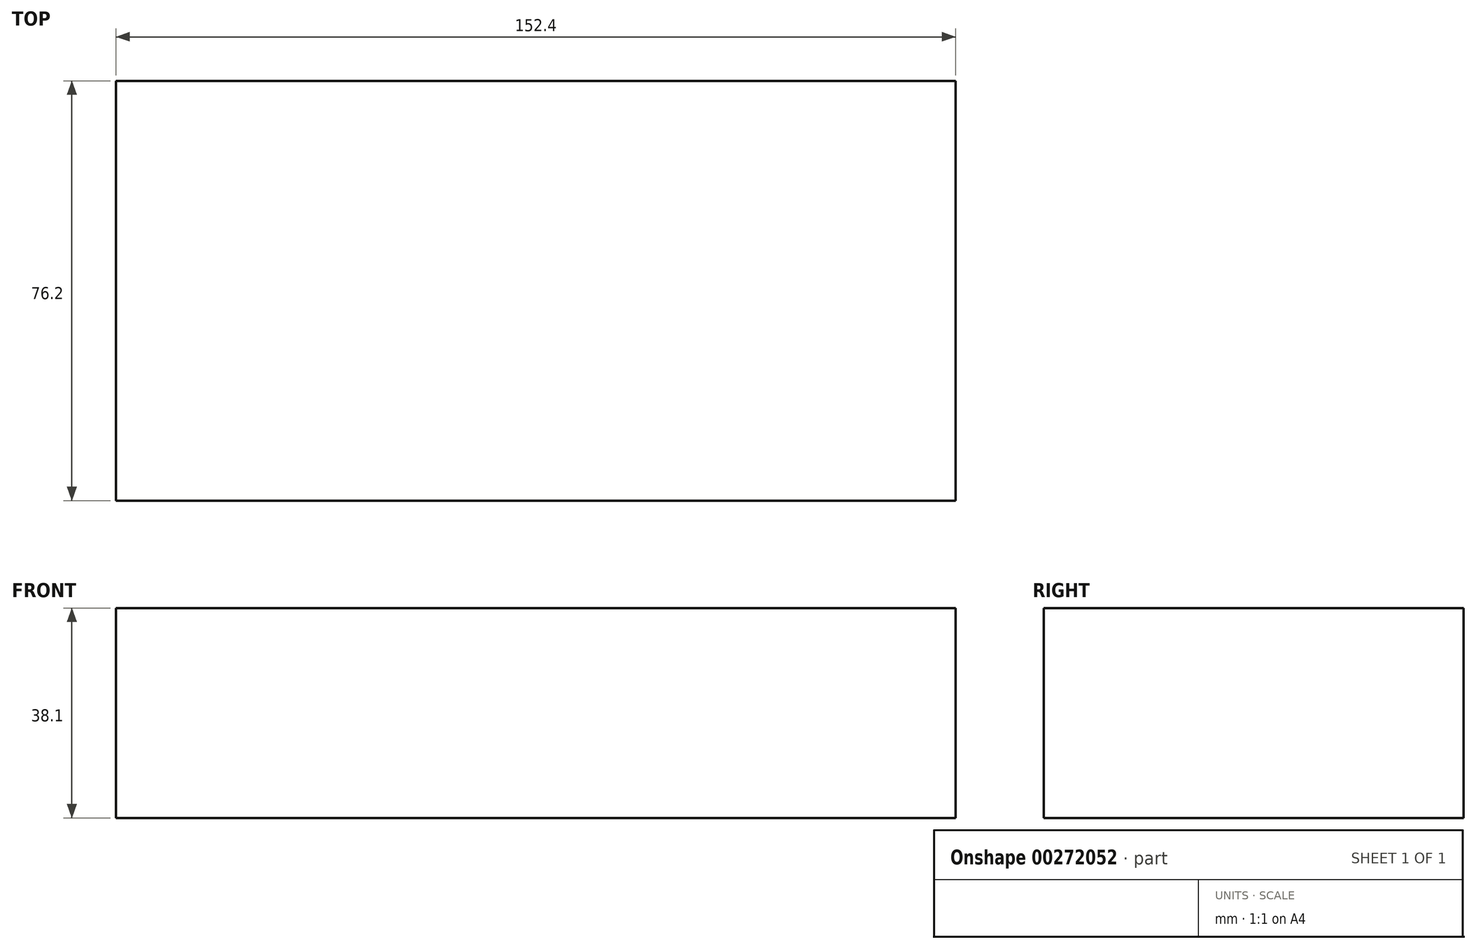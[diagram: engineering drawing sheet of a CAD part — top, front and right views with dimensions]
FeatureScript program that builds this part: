
annotation { "Feature Type Name" : "Feature", "Feature Type Description" : "" }
export const myFeature = defineFeature(function(context is Context, id is Id, definition is map)
    precondition{}
    {
        {
            var Q0;
            Q0=qCreatedBy(makeId("Front.planeOp"),FACE);
            var sketch = newSketch(context, id + "F0", { "sketchPlane" : qUnion([Q0])});
            skLineSegment(sketch, "E0.bottom", {"start": v(-70.73, -5.78) * mm, "end": v(81.67, -5.78) * mm});
            skLineSegment(sketch, "E0.top", {"start": v(-70.73, -43.88) * mm, "end": v(81.67, -43.88) * mm});
            skLineSegment(sketch, "E0.left", {"start": v(-70.73, -5.78) * mm, "end": v(-70.73, -43.88) * mm});
            skLineSegment(sketch, "E0.right", {"start": v(81.67, -5.78) * mm, "end": v(81.67, -43.88) * mm});
            skSolve(sketch);
        }
        {
            var Q0;
            Q0=makeQuery(id+"F0.imprint","IMPRINT",FACE,{"disambiguationData":[TD([[makeQuery(id+"F0.imprint","IMPRINT",EDGE,{"derivedFrom":sQuery(id+"F0.wireOp",EDGE,"E0.bottom")}),-1.0]])]});
            extrude(context, id + "F1", {"entities" : qUnion([Q0]), "depth" : 76.2 * mm});
        }
    });
